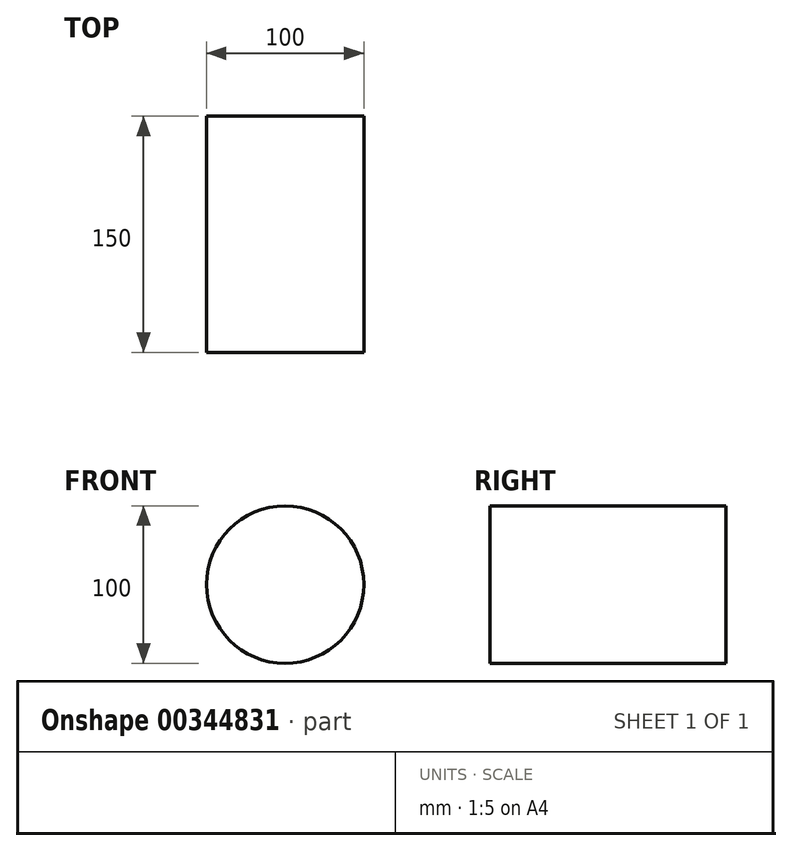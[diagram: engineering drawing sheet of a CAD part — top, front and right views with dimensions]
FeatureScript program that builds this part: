
annotation { "Feature Type Name" : "Feature", "Feature Type Description" : "" }
export const myFeature = defineFeature(function(context is Context, id is Id, definition is map)
    precondition{}
    {
        {
            var Q0;
            Q0=qCreatedBy(makeId("Front.planeOp"),FACE);
            var sketch = newSketch(context, id + "F0", { "sketchPlane" : qUnion([Q0])});
            skCircle(sketch, "E0", {"center": v(0, 0) * mm, "radius": 50 * mm});
            skSolve(sketch);
        }
        {
            var Q0;
            Q0=makeQuery(id+"F0.imprint","IMPRINT",FACE,{"disambiguationData":[TD([[makeQuery(id+"F0.imprint","IMPRINT",EDGE,{"derivedFrom":sQuery(id+"F0.wireOp",EDGE,"E0")}),1.0]])]});
            extrude(context, id + "F1", {"entities" : qUnion([Q0]), "depth" : 150 * mm});
        }
    });
